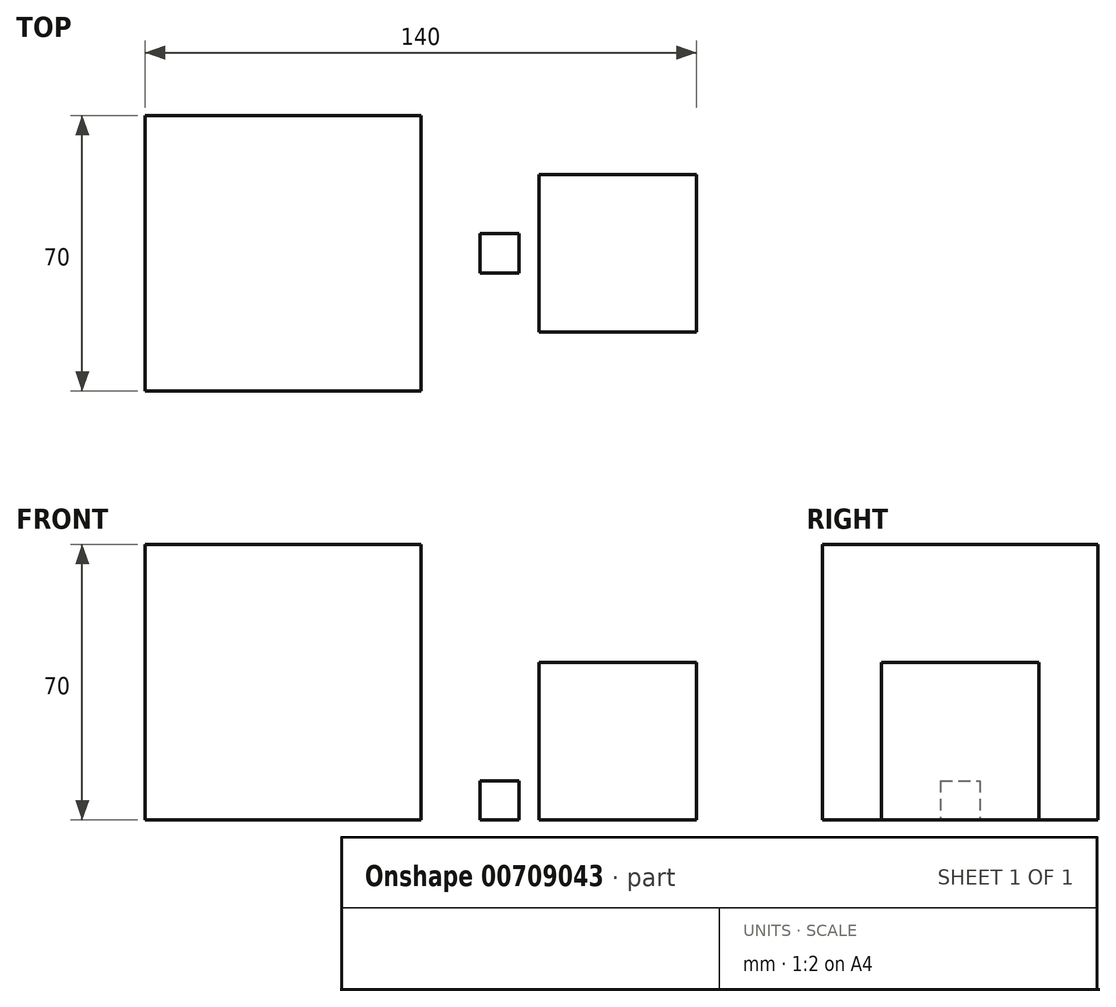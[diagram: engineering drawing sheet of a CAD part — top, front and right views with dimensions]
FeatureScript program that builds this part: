
annotation { "Feature Type Name" : "Feature", "Feature Type Description" : "" }
export const myFeature = defineFeature(function(context is Context, id is Id, definition is map)
    precondition{}
    {
        {
            var Q0;
            Q0=qCreatedBy(makeId("Top.planeOp"),FACE);
            var sketch = newSketch(context, id + "F0", { "sketchPlane" : qUnion([Q0])});
            skLineSegment(sketch, "E0.bottom", {"start": v(5, -5) * mm, "end": v(-5, -5) * mm});
            skLineSegment(sketch, "E0.top", {"start": v(5, 5) * mm, "end": v(-5, 5) * mm});
            skLineSegment(sketch, "E0.left", {"start": v(5, -5) * mm, "end": v(5, 5) * mm});
            skLineSegment(sketch, "E0.right", {"start": v(-5, -5) * mm, "end": v(-5, 5) * mm});
            skPoint(sketch, "E0.middle", {"position": v(0, 0) * mm});
            skLineSegment(sketch, "E1.bottom", {"start": v(50, -20) * mm, "end": v(10, -20) * mm});
            skLineSegment(sketch, "E1.top", {"start": v(50, 20) * mm, "end": v(10, 20) * mm});
            skLineSegment(sketch, "E1.left", {"start": v(50, -20) * mm, "end": v(50, 20) * mm});
            skLineSegment(sketch, "E1.right", {"start": v(10, -20) * mm, "end": v(10, 20) * mm});
            skPoint(sketch, "E1.middle", {"position": v(30, 0) * mm});
            skLineSegment(sketch, "E2.bottom", {"start": v(-20, -35) * mm, "end": v(-90, -35) * mm});
            skLineSegment(sketch, "E2.top", {"start": v(-20, 35) * mm, "end": v(-90, 35) * mm});
            skLineSegment(sketch, "E2.left", {"start": v(-20, -35) * mm, "end": v(-20, 35) * mm});
            skLineSegment(sketch, "E2.right", {"start": v(-90, -35) * mm, "end": v(-90, 35) * mm});
            skPoint(sketch, "E2.middle", {"position": v(-55, 0) * mm});
            skSolve(sketch);
        }
        {
            var Q0;
            Q0=makeQuery(id+"F0.imprint","IMPRINT",FACE,{"disambiguationData":[TD([[makeQuery(id+"F0.imprint","IMPRINT",EDGE,{"derivedFrom":sQuery(id+"F0.wireOp",EDGE,"E2.bottom")}),-1.0]])]});
            extrude(context, id + "F1", {"entities" : qUnion([Q0]), "depth" : 70 * mm, "offsetDistance" : 25.4 * mm});
        }
        {
            var Q0;
            Q0=makeQuery(id+"F0.imprint","IMPRINT",FACE,{"disambiguationData":[TD([[makeQuery(id+"F0.imprint","IMPRINT",EDGE,{"derivedFrom":sQuery(id+"F0.wireOp",EDGE,"E0.bottom")}),-1.0]])]});
            extrude(context, id + "F2", {"entities" : qUnion([Q0]), "depth" : 10 * mm, "offsetDistance" : 25.4 * mm});
        }
        {
            var Q0;
            Q0=makeQuery(id+"F0.imprint","IMPRINT",FACE,{"disambiguationData":[TD([[makeQuery(id+"F0.imprint","IMPRINT",EDGE,{"derivedFrom":sQuery(id+"F0.wireOp",EDGE,"E1.bottom")}),-1.0]])]});
            extrude(context, id + "F3", {"entities" : qUnion([Q0]), "depth" : 40 * mm, "offsetDistance" : 25.4 * mm});
        }
    });
